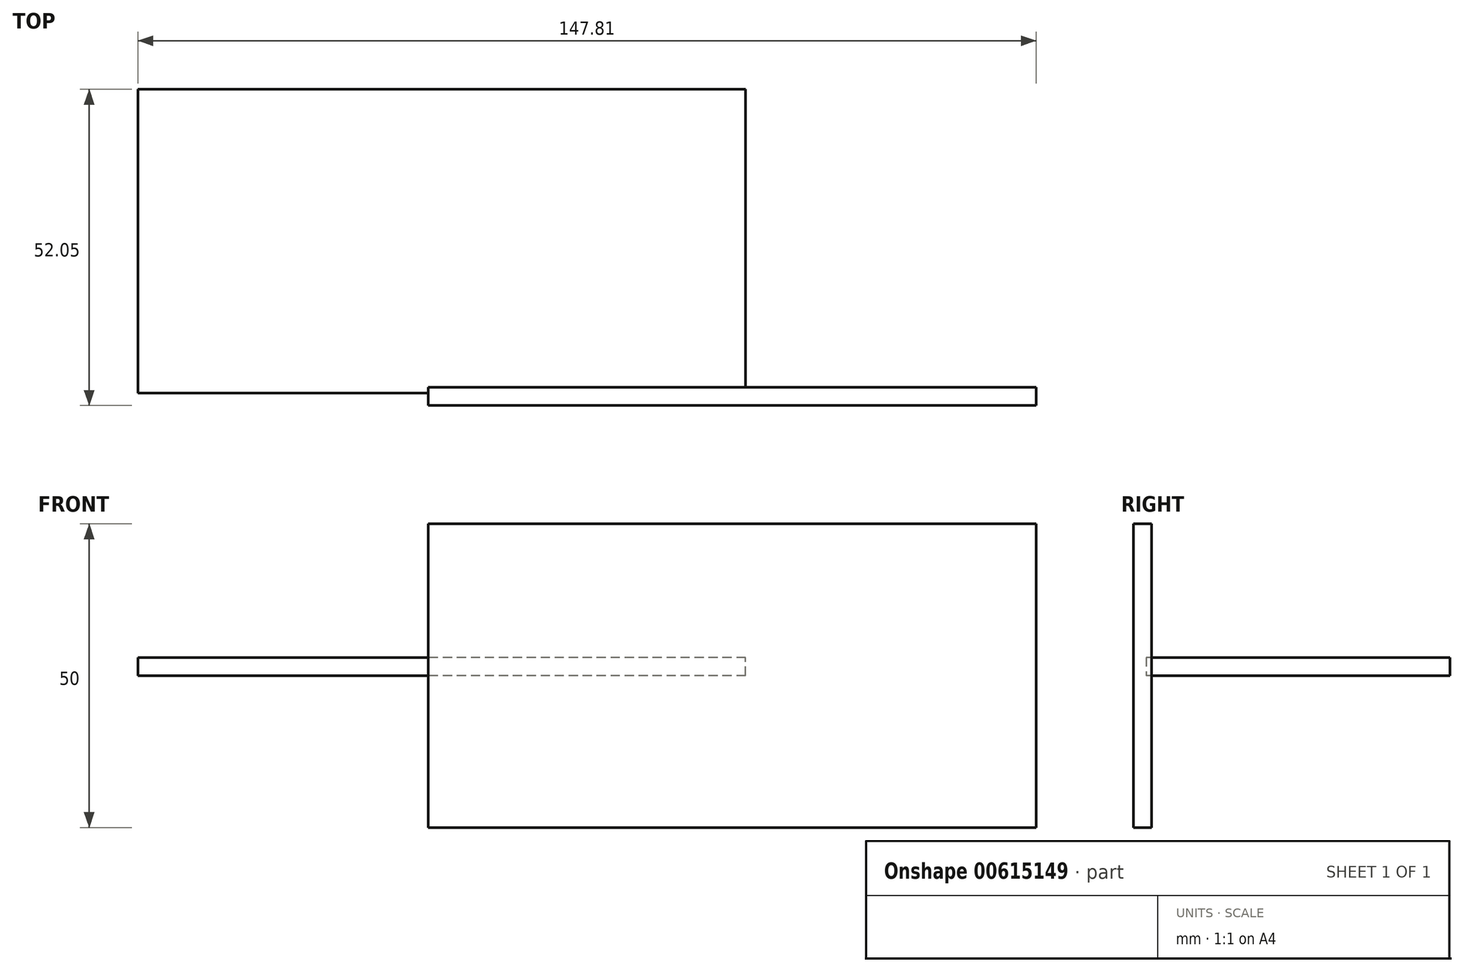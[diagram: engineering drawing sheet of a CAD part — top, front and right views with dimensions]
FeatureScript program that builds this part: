
annotation { "Feature Type Name" : "Feature", "Feature Type Description" : "" }
export const myFeature = defineFeature(function(context is Context, id is Id, definition is map)
    precondition{}
    {
        {
            var Q0;
            Q0=qCreatedBy(makeId("Front.planeOp"),FACE);
            var sketch = newSketch(context, id + "F0", { "sketchPlane" : qUnion([Q0])});
            skLineSegment(sketch, "E0.bottom", {"start": v(-50, 25) * mm, "end": v(50, 25) * mm});
            skLineSegment(sketch, "E0.top", {"start": v(-50, -25) * mm, "end": v(50, -25) * mm});
            skLineSegment(sketch, "E0.left", {"start": v(-50, 25) * mm, "end": v(-50, -25) * mm});
            skLineSegment(sketch, "E0.right", {"start": v(50, 25) * mm, "end": v(50, -25) * mm});
            skPoint(sketch, "E0.middle", {"position": v(0, 0) * mm});
            skPoint(sketch, "E1.middle", {"position": v(-6, -46.78) * mm});
            skSolve(sketch);
        }
        {
            var Q0;
            Q0 = qSketchRegion(id + "F0", true);
            extrude(context, id + "F1", {"entities" : qUnion([Q0]), "depth" : 3 * mm, "offsetDistance" : 25 * mm});
        }
        {
            var Q0;
            Q0=qCreatedBy(makeId("Top.planeOp"),FACE);
            var sketch = newSketch(context, id + "F2", { "sketchPlane" : qUnion([Q0])});
            skLineSegment(sketch, "E2.bottom", {"start": v(2.2, 49.05) * mm, "end": v(-97.8, 49.05) * mm});
            skLineSegment(sketch, "E2.top", {"start": v(2.2, -0.95) * mm, "end": v(-97.8, -0.95) * mm});
            skLineSegment(sketch, "E2.left", {"start": v(2.2, 49.05) * mm, "end": v(2.2, -0.95) * mm});
            skLineSegment(sketch, "E2.right", {"start": v(-97.8, 49.05) * mm, "end": v(-97.8, -0.95) * mm});
            skSolve(sketch);
        }
        {
            var Q0;
            Q0 = qSketchRegion(id + "F2", true);
            extrude(context, id + "F3", {"entities" : qUnion([Q0]), "operationType" : NewBodyOperationType.ADD, "depth" : 3 * mm, "offsetDistance" : 25 * mm});
        }
    });
